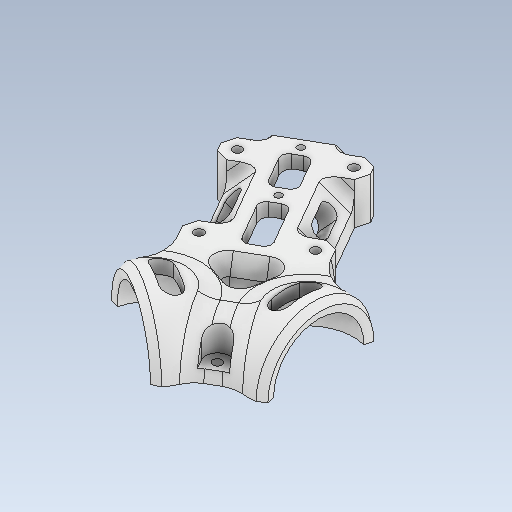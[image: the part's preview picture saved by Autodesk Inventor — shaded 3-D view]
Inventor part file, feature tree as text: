
AUTODESK INVENTOR PART (.ipt)
format: ipt  version: 2020 (Build 240168000, 168)  size: 811,520 bytes
history: native  units: mm
features: sketch x14, extrude x12, projected_geometry x12, thicken_offset x5, chamfer x4, fillet x4, other x4, revolve x2, plane x2, mirror x2, reference x1
ambient origin geometry x8: Origin, YZ Plane, XZ Plane, XY Plane, X Axis, Y Axis, Z Axis, Center Point
bodies: Solid1 (feature_tree)
feature tree (62):
  revolve  "Revolution1"  [1 undecoded]
  thicken_offset  "Thicken1"
  revolve  "Revolution2"  [1 undecoded]
  extrude  "Extrusion1"  Depth=27.0mm
  extrude  "Extrusion2"  Depth=3.0mm
  plane  "Work Plane1"
  extrude  "Extrusion3"  Depth=12.0mm
  extrude  "Extrusion4"  TaperAngle=180.0deg  [1 undecoded]
  thicken_offset  "Thicken2"
  extrude  "Extrusion5"  Depth=1.5mm
  mirror  "Mirror1"
  chamfer  "Chamfer2"  Distance=5.0mm
  chamfer  "Chamfer3"  Distance=18.0mm
  extrude  "Extrusion6"  Depth=2.0mm
  extrude  "Extrusion7"  Depth=2.0mm TaperAngle=0.0deg
  fillet  "Fillet1"  [1 undecoded]
  fillet  "Fillet2"  Radius=20.0mm
  thicken_offset  "Thicken3"
  thicken_offset  "Thicken4"
  extrude  "Extrusion8"  Depth=20.0mm
  thicken_offset  "Thicken5"
  plane  "Work Plane2"
  extrude  "Extrusion9"  Depth=8.0mm
  fillet  "Fillet3"  Radius=12.0mm
  extrude  "Extrusion11"  Depth=20.0mm
  extrude  "Extrusion12"  Depth=8.0mm
  chamfer  "Chamfer4"  Distance=12.0mm
  fillet  "Fillet4"  Radius=60.0mm
  extrude  "Extrusion13"  Depth=2.0mm TaperAngle=0.0deg
  mirror  "Mirror2"
  chamfer  "Chamfer5"  Distance=5.0mm
  sketch  "Sketch1"  dims[d0=40.0mm d1=54.0mm]
  sketch  "Sketch2"  dims[d2=27.0mm d3=27.0mm]
  reference  "Reference1"
  projected_geometry  "Projected Loop1"
  sketch  "Sketch3"  dims[d4=105.0deg d5=27.0mm]
  projected_geometry  "Projected Loop2"
  sketch  "Sketch4"  dims[d6=105.0deg d7=3.0mm]
  projected_geometry  "Projected Loop3"
  sketch  "Sketch5"  dims[d8=3.0mm d9=12.0mm]
  projected_geometry  "Projected Loop4"
  sketch  "Sketch6"  dims[d10=0.0mm d11=180.0deg]
  projected_geometry  "Projected Loop5"
  sketch  "Sketch7"  dims[d12=1.5mm d13=1.5mm]
  projected_geometry  "Projected Loop6"
  sketch  "Sketch8"  dims[d14=70.0mm]
  projected_geometry  "Projected Loop7"
  sketch  "Sketch9"  dims[d15=180.0deg]
  projected_geometry  "Projected Loop8"
  sketch  "Sketch10"  dims[d16=80.0mm]
  projected_geometry  "Projected Loop9"
  sketch  "Sketch11"  dims[d17=40.0mm]
  projected_geometry  "Projected Loop10"
  sketch  "Sketch13"  dims[d18=80.0mm]
  projected_geometry  "Projected Loop12"
  sketch  "Sketch15"  dims[d19=4.0mm]
  sketch  "Sketch16"  dims[d20=8.0mm d21=5.0mm d22=18.0mm d23=0.0mm d24=25.0mm d25=60.0mm d26=0.0mm d27=-20.0mm d28=20.0mm d29=20.0mm d30=8.0mm d31=12.0mm d32=20.0mm d33=8.0mm d34=12.0mm d35=60.0mm d36=0.0mm d37=60.0mm d38=0.0mm d39=5.0mm d40=5.0mm d41=4.0mm d42=6.0mm d43=4.0mm d44=60.0mm d45=0.0mm d49=10.0mm d50=2.0mm d51=45.0deg d52=8.0mm d53=2.0mm d54=45.0deg d55=5.0mm d56=4.0mm d57=60.0mm d58=0.0mm d59=24.0mm d60=4.0mm d61=12.0mm d62=10.0mm d63=10.0mm d64=60.0mm d65=0.0mm d66=2.0mm d67=12.0mm d68=2.0mm d69=2.0mm d70=2.0mm d71=2.0mm d72=13.0mm d73=13.0mm d74=18.0mm d75=10.0mm d76=18.0mm d77=10.0mm d78=3.0mm d79=3.0mm d80=60.0mm d81=0.0mm d82=5.0mm d83=5.0mm d84=-5.0mm d85=12.0mm d86=10.0mm d87=60.0mm d88=0.0mm d89=12.0mm d96=3.0mm d97=3.0mm d98=50.0mm d99=0.0mm d108=5.0mm d109=6.0mm d110=8.0mm d111=50.0mm d112=0.0mm d113=4.0mm d114=2.0mm d115=45.0deg d116=4.0mm d117=5.0mm d118=7.0mm d119=50.0mm d120=0.0mm d121=4.0mm d122=2.0mm d123=60.0deg]
  projected_geometry  "Projected Loop14"
  parser-record x1  (decoder bookkeeping rows leaked as tree rows — omitted from the tree; the rows remain in map.json)
  other  "leg_1.iam"
  other  "sub_leg_1_lit:1"
  other  "carbon_fiber_25_21_300:1"
note: 4 required parameter values undecoded (feature->parameter linkage not recoverable at this tier; creation-order binding heuristic only, values carry confidence <= 0.55)
note: 1 file-system path scrubbed to <path> (originals preserved in map.json)